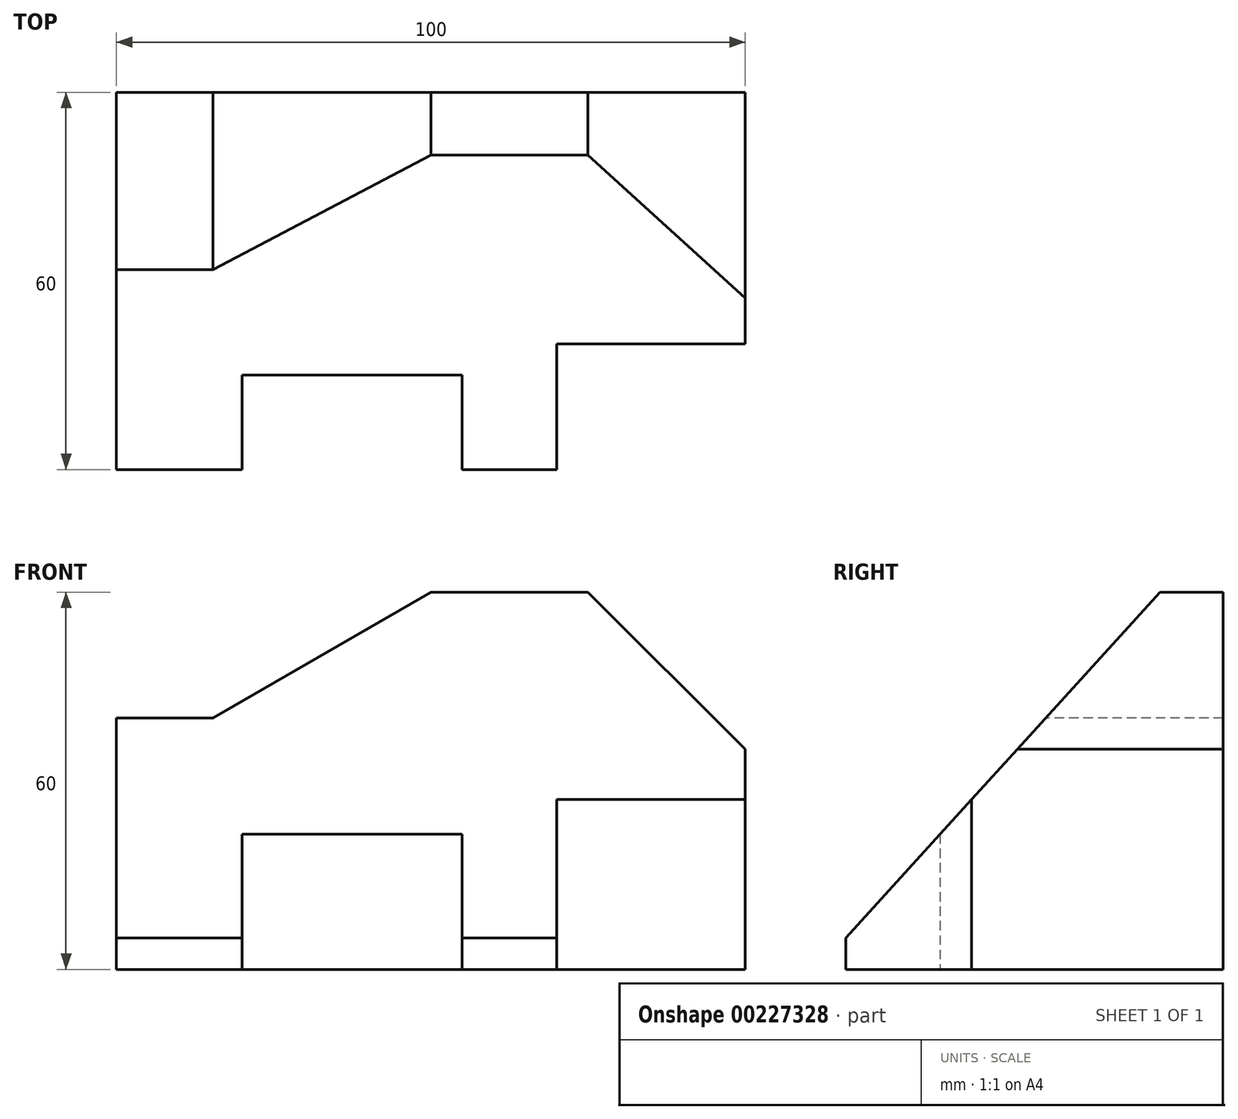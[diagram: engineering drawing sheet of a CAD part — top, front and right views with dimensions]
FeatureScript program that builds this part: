
annotation { "Feature Type Name" : "Feature", "Feature Type Description" : "" }
export const myFeature = defineFeature(function(context is Context, id is Id, definition is map)
    precondition{}
    {
        {
            var Q0;
            Q0=qCreatedBy(makeId("Top.planeOp"),FACE);
            var sketch = newSketch(context, id + "F0", { "sketchPlane" : qUnion([Q0])});
            skLineSegment(sketch, "E0", {"start": v(0, 0) * mm, "end": v(20, 0) * mm});
            skLineSegment(sketch, "E1", {"start": v(20, 0) * mm, "end": v(20, 15) * mm});
            skLineSegment(sketch, "E2", {"start": v(20, 15) * mm, "end": v(55, 15) * mm});
            skLineSegment(sketch, "E3", {"start": v(55, 15) * mm, "end": v(55, 0) * mm});
            skLineSegment(sketch, "E4", {"start": v(55, 0) * mm, "end": v(70, 0) * mm});
            skLineSegment(sketch, "E5", {"start": v(70, 0) * mm, "end": v(70, 20) * mm});
            skLineSegment(sketch, "E6", {"start": v(70, 20) * mm, "end": v(100, 20) * mm});
            skLineSegment(sketch, "E7", {"start": v(100, 20) * mm, "end": v(100, 60) * mm});
            skLineSegment(sketch, "E8", {"start": v(100, 60) * mm, "end": v(0, 60) * mm});
            skLineSegment(sketch, "E9", {"start": v(0, 60) * mm, "end": v(0, 0) * mm});
            skSolve(sketch);
        }
        {
            var Q0;
            Q0=makeQuery(id+"F0.imprint","IMPRINT",FACE,{"disambiguationData":[TD([[makeQuery(id+"F0.imprint","IMPRINT",EDGE,{"derivedFrom":sQuery(id+"F0.wireOp",EDGE,"E0")}),1.0]])]});
            extrude(context, id + "F1", {"entities" : qUnion([Q0]), "depth" : 60 * mm});
        }
        {
            var Q0;
            Q0=qCreatedBy(makeId("Front.planeOp"),FACE);
            var sketch = newSketch(context, id + "F2", { "sketchPlane" : qUnion([Q0])});
            skLineSegment(sketch, "E10.0", {"start": v(20, 60) * mm, "end": v(55, 60) * mm, "construction": true});
            skPoint(sketch, "E11.0", {"position": v(62.5, 60) * mm});
            skLineSegment(sketch, "E12.0", {"start": v(70, 60) * mm, "end": v(100, 60) * mm, "construction": true});
            skLineSegment(sketch, "E13.0", {"start": v(0, 60) * mm, "end": v(20, 60) * mm, "construction": true});
            skLineSegment(sketch, "E14.0", {"start": v(0, 0) * mm, "end": v(20, 0) * mm, "construction": true});
            skLineSegment(sketch, "E15.0", {"start": v(20, 0) * mm, "end": v(55, 0) * mm, "construction": true});
            skLineSegment(sketch, "E16.0", {"start": v(55, 0) * mm, "end": v(70, 0) * mm, "construction": true});
            skLineSegment(sketch, "E17.0", {"start": v(70, 0) * mm, "end": v(100, 0) * mm, "construction": true});
            skLineSegment(sketch, "E18", {"start": v(50, 60) * mm, "end": v(15.36, 40) * mm});
            skLineSegment(sketch, "E19", {"start": v(15.36, 40) * mm, "end": v(0, 40) * mm});
            skLineSegment(sketch, "E20", {"start": v(0, 40) * mm, "end": v(0, 60) * mm});
            skLineSegment(sketch, "E21", {"start": v(0, 60) * mm, "end": v(50, 60) * mm});
            skLineSegment(sketch, "E22.0", {"start": v(100, 60) * mm, "end": v(100, 0) * mm, "construction": true});
            skLineSegment(sketch, "E23", {"start": v(75, 60) * mm, "end": v(100, 35) * mm});
            skLineSegment(sketch, "E24", {"start": v(100, 35) * mm, "end": v(100, 60) * mm});
            skLineSegment(sketch, "E25", {"start": v(75, 60) * mm, "end": v(100, 60) * mm});
            skSolve(sketch);
        }
        {
            var Q0;
            Q0=makeQuery(id+"F2.imprint","IMPRINT",FACE,{"disambiguationData":[TD([[makeQuery(id+"F2.imprint","IMPRINT",EDGE,{"derivedFrom":sQuery(id+"F2.wireOp",EDGE,"E18")}),-1.0]])]});
            var Q1;
            Q1=makeQuery(id+"F2.imprint","IMPRINT",FACE,{"disambiguationData":[TD([[makeQuery(id+"F2.imprint","IMPRINT",EDGE,{"derivedFrom":sQuery(id+"F2.wireOp",EDGE,"E23")}),1.0]])]});
            extrude(context, id + "F3", {"entities" : qUnion([Q0, Q1]), "operationType" : NewBodyOperationType.REMOVE, "endBound" : BoundingType.THROUGH_ALL, "oppositeDirection" : true, "depth" : 86 * mm});
        }
        {
            var Q0;
            Q0=makeQuery(id+"F1.opExtrude","SWEPT_FACE",FACE,{"disambiguationData":[OSD([sQuery(id+"F0.wireOp",EDGE,"E7")])]});
            var sketch = newSketch(context, id + "F4", { "sketchPlane" : qUnion([Q0])});
            skLineSegment(sketch, "E26.0", {"start": v(60, 60) * mm, "end": v(20, 60) * mm, "construction": true});
            skLineSegment(sketch, "E27.0", {"start": v(0, 60) * mm, "end": v(20, 60) * mm, "construction": true});
            skLineSegment(sketch, "E28.0.0", {"start": v(0, 0) * mm, "end": v(20, 0) * mm, "construction": true});
            skLineSegment(sketch, "E28.0.1", {"start": v(20, 0) * mm, "end": v(20, 60) * mm, "construction": true});
            skLineSegment(sketch, "E28.0.2", {"start": v(20, 60) * mm, "end": v(0, 60) * mm, "construction": true});
            skLineSegment(sketch, "E28.0.3", {"start": v(0, 60) * mm, "end": v(0, 0) * mm, "construction": true});
            skLineSegment(sketch, "E29", {"start": v(50, 60) * mm, "end": v(0, 60) * mm});
            skLineSegment(sketch, "E30", {"start": v(0, 5) * mm, "end": v(50, 60) * mm});
            skLineSegment(sketch, "E31", {"start": v(0, 60) * mm, "end": v(0, 5) * mm});
            skSolve(sketch);
        }
        {
            var Q0;
            Q0 = qSketchRegion(id + "F4", true);
            extrude(context, id + "F5", {"entities" : qUnion([Q0]), "operationType" : NewBodyOperationType.REMOVE, "endBound" : BoundingType.THROUGH_ALL, "oppositeDirection" : true, "depth" : 25 * mm});
        }
        {
            var Q0;
            {var subQ2=sQuery(id+"F4.wireOp",EDGE,"E29");Q0=makeQuery(id+"F4.imprint","IMPRINT",FACE,{"disambiguationData":[TD([[makeQuery(id+"F4.imprint","IMPRINT",EDGE,{"derivedFrom":subQ2}),1.0]])]});}
            extrude(context, id + "F6", {"entities" : qUnion([Q0]), "operationType" : NewBodyOperationType.REMOVE, "endBound" : BoundingType.THROUGH_ALL, "oppositeDirection" : true, "depth" : 25 * mm});
        }
    });
